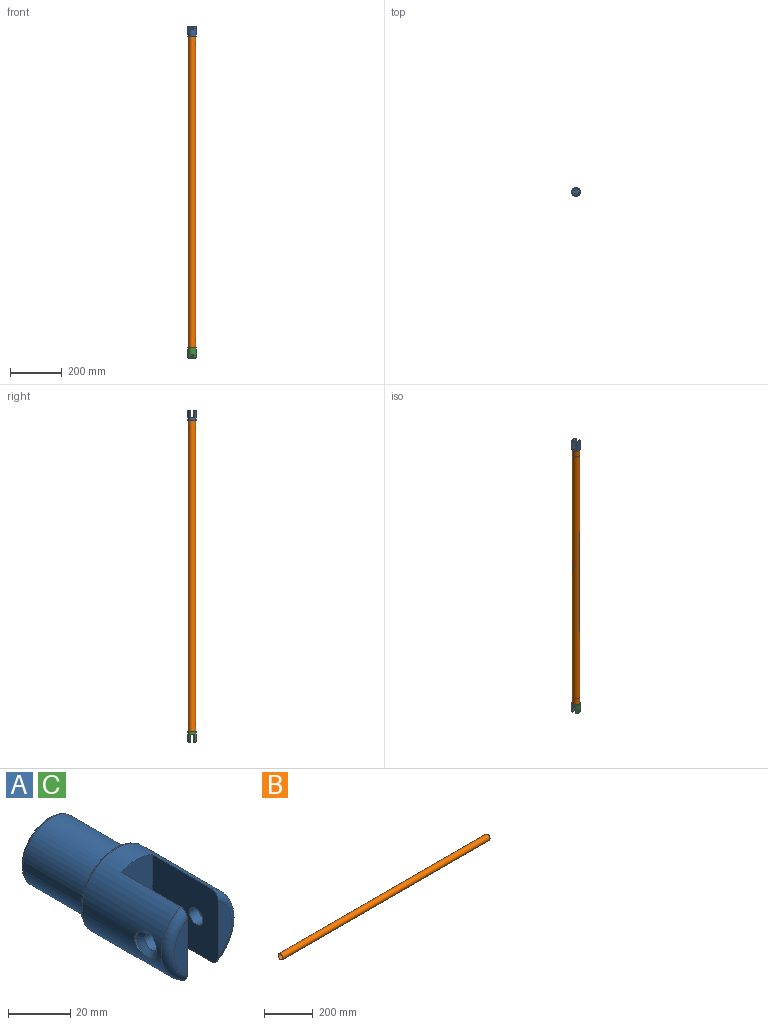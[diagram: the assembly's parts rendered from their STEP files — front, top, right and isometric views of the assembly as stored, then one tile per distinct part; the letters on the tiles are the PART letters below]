
ASSEMBLY  parts=3 mates=5
PART A: 23 faces, bbox 34.6x70x34.6 mm
  f0: cylinder r=16mm len=36mm, axis (0,1,0), area 2677.7mm2, adj f8,f9,f10,f11,f12,f13,f18,f19
  f1: cylinder r=3.1mm len=6.2mm, axis (1,0,0), area 77.9mm2, adj f9,f22
  f2: cylinder r=3.1mm len=6.3mm, axis (1,0,0), area 122.7mm2, adj f10,f20
  f3: plane 21.91x6mm, normal (0,-1,0), area 92.7mm2, adj f9,f12
  f4: cylinder r=12.9mm len=28mm, axis (0,-1,0), area 2269.5mm2, adj f14,f15
  f5: plane 23.8x23.8mm, normal (0,1,0), area 130.7mm2, adj f14,f16
  f6: plane 21.91x6mm, normal (0,-1,0), area 92.7mm2, adj f10,f11
  f7: plane 30x30mm, normal (0,1,0), area 99.9mm2, adj f13,f15
  f8: plane 32x14mm, normal (0,-1,0), area 433.3mm2, adj f0,f9,f10
  f9: plane 30x28.78mm, normal (-1,0,0), area 828.7mm2, adj f0,f1,f3,f8,f12
  f10: plane 30x28.78mm, normal (1,0,0), area 828.7mm2, adj f0,f2,f6,f8,f11
  f11: torus R=13mm, axis (0,-1,0), area 152mm2, adj f0,f6,f10
  f12: torus R=13mm, axis (0,-1,0), area 152mm2, adj f0,f3,f9
  f13: torus R=15mm, axis (0,-1,0), area 154.3mm2, adj f0,f7
  f14: torus R=11.9mm, axis (0,-1,0), area 123.7mm2, adj f4,f5
  f15: torus R=13.9mm, axis (0,-1,0), area 130.9mm2, adj f4,f7
  f16: cylinder r=10mm len=25mm, axis (0,1,0), area 1570.8mm2, adj f5,f17
  f17: plane 20x20mm, normal (0,1,0), area 314.2mm2, adj f16
  f18: cylinder r=5mm len=10mm, axis (-1,0,0), area 6.3mm2, adj f0,f20
  f19: cylinder r=5mm len=10mm, axis (-1,0,0), area 6.3mm2, adj f0,f20
  f20: cone r=3.05mm half-angle=45deg, axis (-1,0,0), area 68.4mm2, adj f2,f18,f19
  f21: cylinder r=5mm len=10mm, axis (1,0,0), area 144.6mm2, adj f0,f22
  f22: plane 10x10mm, normal (1,0,0), area 48.3mm2, adj f1,f21
PART B: 4 faces, bbox 1200x28x28 mm
  f0: cylinder r=13mm len=1200mm, axis (-1,0,0), area 98017.7mm2, adj f2,f3
  f1: cylinder r=14mm len=1200mm, axis (-1,0,0), area 105557.5mm2, adj f2,f3
  f2: plane 28x28mm, normal (1,0,0), area 84.8mm2, adj f0,f1
  f3: plane 28x28mm, normal (-1,0,0), area 84.8mm2, adj f0,f1
PART C: same geometry as A
PLACE A rot(axis=(-0.65,0.54,-0.54),113.7deg) t=(45.28,416.71,467.16)mm
PLACE B rot(axis=(-0.58,-0.58,-0.58),120deg) t=(-193.81,360.75,-731.84)mm
PLACE C rot(axis=(0.5,0.61,0.61),126.7deg) t=(45.28,416.71,-730.84)mm
MATE planar B.f0 <-> C.f0  axis (0,0,-1) through (45.28,416.71,-731.84)mm
MATE cylindrical C.f4 <-> B.f0  axis (0,0,-1) through (45.28,416.71,-715.84)mm
MATE cylindrical A.f4 <-> B.f0  axis (0,0,1) through (45.28,416.71,452.16)mm
MATE planar B.f0 <-> A.f0  axis (0,0,1) through (45.28,416.71,468.16)mm
MATE parallel C.f10 <-> A.f10  axis (-0.2,0.98,0) through (46.64,409.84,-755.58)mm
